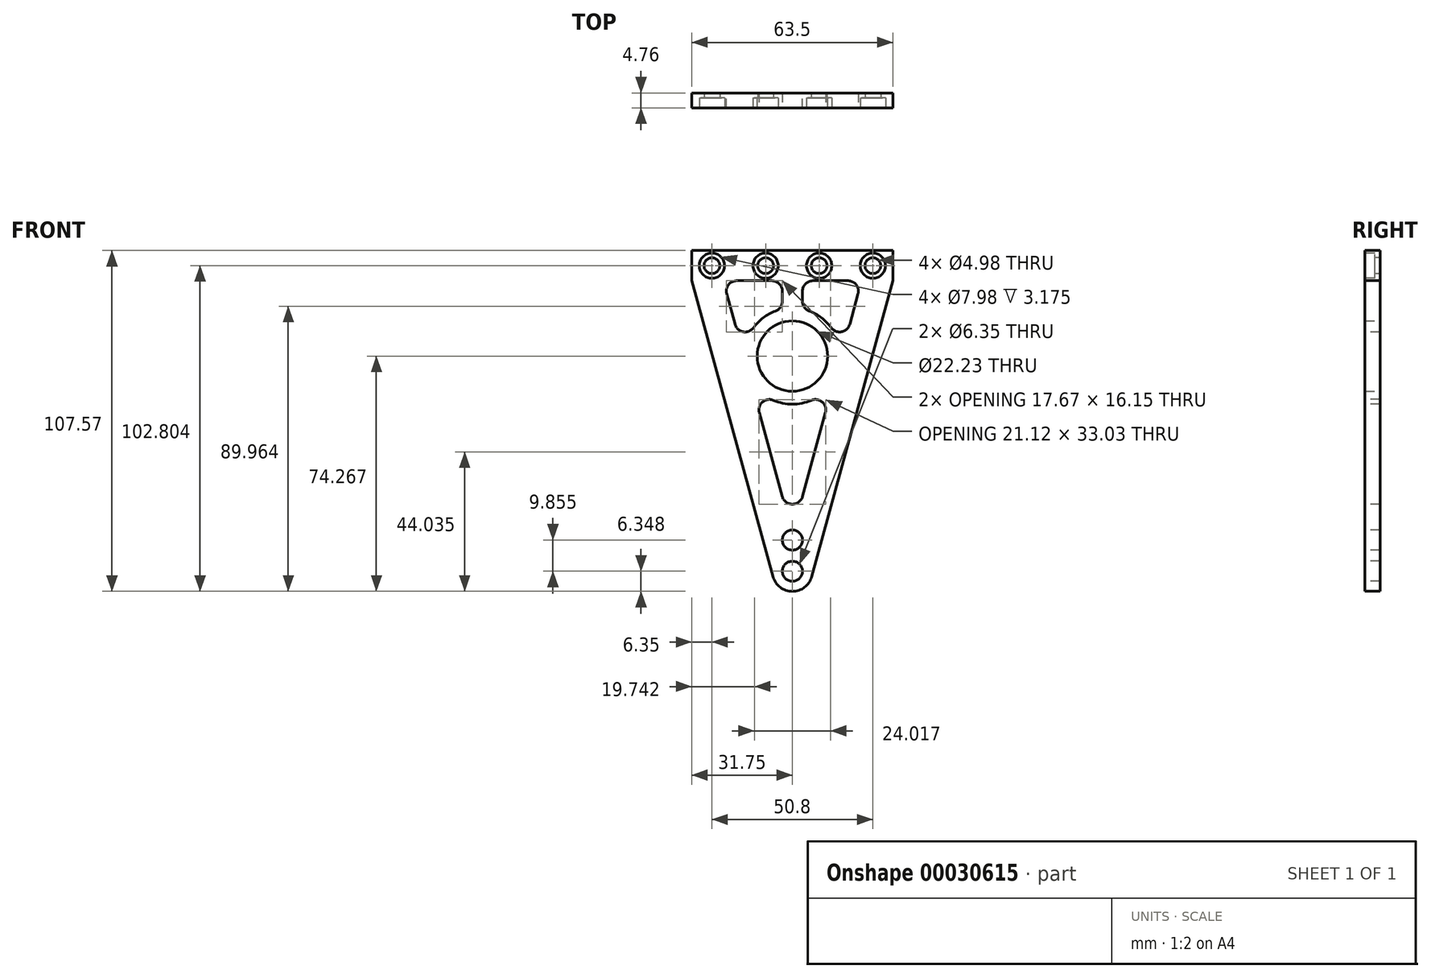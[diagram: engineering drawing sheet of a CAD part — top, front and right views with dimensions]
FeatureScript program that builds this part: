
annotation { "Feature Type Name" : "Feature", "Feature Type Description" : "" }
export const myFeature = defineFeature(function(context is Context, id is Id, definition is map)
    precondition{}
    {
        {
            var Q0;
            Q0=qCreatedBy(makeId("Front.planeOp"),FACE);
            var sketch = newSketch(context, id + "F0", { "sketchPlane" : qUnion([Q0])});
            skLineSegment(sketch, "E0.rect.bottom", {"start": v(31.75, 39.32) * mm, "end": v(-31.75, 39.32) * mm});
            skLineSegment(sketch, "E0.rect.left", {"start": v(31.75, 39.32) * mm, "end": v(31.75, 29.8) * mm});
            skLineSegment(sketch, "E0.rect.right", {"start": v(-31.75, 39.32) * mm, "end": v(-31.75, 29.8) * mm});
            skPoint(sketch, "E0.rect.middle", {"position": v(0, 0) * mm});
            skArc(sketch, "E1", {"start": v(-6.12, -63.58) * mm, "mid": v(0, -68.25) * mm, "end": v(6.12, -63.58) * mm});
            skLineSegment(sketch, "E2", {"start": v(-31.75, 29.8) * mm, "end": v(-6.12, -63.58) * mm});
            skLineSegment(sketch, "E3", {"start": v(31.75, 29.8) * mm, "end": v(6.12, -63.58) * mm});
            skPoint(sketch, "E4.orphan", {"position": v(-31.75, -39.32) * mm});
            skPoint(sketch, "E5.orphan", {"position": v(31.75, -39.32) * mm});
            skCircle(sketch, "E6", {"center": v(0, 6.02) * mm, "radius": 11.11 * mm});
            skPoint(sketch, "E7.orphan", {"position": v(0, 39.32) * mm});
            skSolve(sketch);
        }
        {
            var Q0;
            Q0 = qSketchRegion(id + "F0", true);
            extrude(context, id + "F1", {"entities" : qUnion([Q0]), "depth" : 4.76 * mm});
        }
        {
            var Q0;
            Q0=makeQuery(id+"F1.opExtrude","CAP_FACE",FACE,{"disambiguationData":[OSD([sQuery(id+"F0.wireOp",EDGE,"E0.rect.bottom"),sQuery(id+"F0.wireOp",EDGE,"E0.rect.left"),sQuery(id+"F0.wireOp",EDGE,"E0.rect.right"),sQuery(id+"F0.wireOp",EDGE,"E1"),sQuery(id+"F0.wireOp",EDGE,"E2"),sQuery(id+"F0.wireOp",EDGE,"E3"),sQuery(id+"F0.wireOp",EDGE,"E6")])],"isStart":false});
            var sketch = newSketch(context, id + "F2", { "sketchPlane" : qUnion([Q0])});
            skLineSegment(sketch, "E8.0", {"start": v(-21.87, 29.8) * mm, "end": v(-15.16, 5.34) * mm});
            skLineSegment(sketch, "E9.0", {"start": v(21.87, 29.8) * mm, "end": v(15.16, 5.34) * mm});
            skLineSegment(sketch, "E10.0", {"start": v(21.87, 29.8) * mm, "end": v(3.17, 29.8) * mm});
            skArc(sketch, "E11.0", {"start": v(15.16, 5.34) * mm, "mid": v(12.01, 15.3) * mm, "end": v(3.17, 20.86) * mm});
            skLineSegment(sketch, "E12.trimOffspring", {"start": v(13.38, -1.14) * mm, "end": v(0, -49.9) * mm});
            skLineSegment(sketch, "E13.trimOffspring", {"start": v(-13.38, -1.14) * mm, "end": v(0, -49.9) * mm});
            skArc(sketch, "E14.trimOffspring", {"start": v(-13.38, -1.14) * mm, "mid": v(0, -9.16) * mm, "end": v(13.38, -1.14) * mm});
            skLineSegment(sketch, "E15.rect.left", {"start": v(3.17, 18.15) * mm, "end": v(3.17, 29.8) * mm});
            skLineSegment(sketch, "E15.rect.right", {"start": v(-3.18, 20.86) * mm, "end": v(-3.18, 29.8) * mm});
            skPoint(sketch, "E15.rect.middle", {"position": v(0, 29.8) * mm});
            skPoint(sketch, "E16.orphan", {"position": v(3.17, 41.43) * mm});
            skPoint(sketch, "E17.orphan", {"position": v(-3.18, 41.43) * mm});
            skLineSegment(sketch, "E18.trimOffspring", {"start": v(-3.18, 29.8) * mm, "end": v(-21.87, 29.8) * mm});
            skPoint(sketch, "E15.rect.bottom.end.orphan", {"position": v(-3.18, 18.15) * mm});
            skArc(sketch, "E19.trimOffspring", {"start": v(-3.18, 20.86) * mm, "mid": v(-12.01, 15.3) * mm, "end": v(-15.16, 5.34) * mm});
            skSolve(sketch);
        }
        {
            var Q0;
            Q0=makeQuery(id+"F2.imprint","IMPRINT",FACE,{"disambiguationData":[TD([[makeQuery(id+"F2.imprint","IMPRINT",EDGE,{"derivedFrom":sQuery(id+"F2.wireOp",EDGE,"E8.0")}),1.0]])]});
            var Q1;
            Q1=makeQuery(id+"F2.imprint","IMPRINT",FACE,{"disambiguationData":[TD([[makeQuery(id+"F2.imprint","IMPRINT",EDGE,{"derivedFrom":sQuery(id+"F2.wireOp",EDGE,"E9.0")}),-1.0]])]});
            var Q2;
            Q2=makeQuery(id+"F2.imprint","IMPRINT",FACE,{"disambiguationData":[TD([[makeQuery(id+"F2.imprint","IMPRINT",EDGE,{"derivedFrom":sQuery(id+"F2.wireOp",EDGE,"E12.trimOffspring")}),-1.0]])]});
            extrude(context, id + "F3", {"entities" : qUnion([Q0, Q1, Q2]), "operationType" : NewBodyOperationType.REMOVE, "endBound" : BoundingType.THROUGH_ALL, "oppositeDirection" : true, "depth" : 25.4 * mm});
        }
        {
            var Q0;
            Q0=makeQuery(id+"F3.boolean.opBoolean","COPY",EDGE,{"derivedFrom":makeQuery(id+"F3.opExtrude","SWEPT_EDGE",EDGE,{"disambiguationData":[OSD([sQuery(id+"F2.wireOp",EDGE,"E8.0"),sQuery(id+"F2.wireOp",EDGE,"E18.trimOffspring")])]})});
            var Q1;
            Q1=makeQuery(id+"F3.boolean.opBoolean","COPY",EDGE,{"derivedFrom":makeQuery(id+"F3.opExtrude","SWEPT_EDGE",EDGE,{"disambiguationData":[OSD([sQuery(id+"F2.wireOp",EDGE,"E10.0"),sQuery(id+"F2.wireOp",EDGE,"E15.rect.left")])]})});
            var Q2;
            Q2=makeQuery(id+"F3.boolean.opBoolean","COPY",EDGE,{"derivedFrom":makeQuery(id+"F3.opExtrude","SWEPT_EDGE",EDGE,{"disambiguationData":[OSD([sQuery(id+"F2.wireOp",EDGE,"E15.rect.right"),sQuery(id+"F2.wireOp",EDGE,"E18.trimOffspring")])]})});
            var Q3;
            Q3=makeQuery(id+"F3.boolean.opBoolean","COPY",EDGE,{"derivedFrom":makeQuery(id+"F3.opExtrude","SWEPT_EDGE",EDGE,{"disambiguationData":[OSD([sQuery(id+"F2.wireOp",EDGE,"E9.0"),sQuery(id+"F2.wireOp",EDGE,"E10.0")])]})});
            var Q4;
            Q4=makeQuery(id+"F3.boolean.opBoolean","COPY",EDGE,{"derivedFrom":makeQuery(id+"F3.opExtrude","SWEPT_EDGE",EDGE,{"disambiguationData":[OSD([sQuery(id+"F2.wireOp",EDGE,"E11.0"),sQuery(id+"F2.wireOp",EDGE,"E15.rect.left")])]})});
            var Q5;
            Q5=makeQuery(id+"F3.boolean.opBoolean","COPY",EDGE,{"derivedFrom":makeQuery(id+"F3.opExtrude","SWEPT_EDGE",EDGE,{"disambiguationData":[OSD([sQuery(id+"F2.wireOp",EDGE,"E15.rect.right"),sQuery(id+"F2.wireOp",EDGE,"E19.trimOffspring")])]})});
            var Q6;
            Q6=makeQuery(id+"F3.boolean.opBoolean","COPY",EDGE,{"derivedFrom":makeQuery(id+"F3.opExtrude","SWEPT_EDGE",EDGE,{"disambiguationData":[OSD([sQuery(id+"F2.wireOp",EDGE,"E9.0"),sQuery(id+"F2.wireOp",EDGE,"E11.0")])]})});
            var Q7;
            Q7=makeQuery(id+"F3.boolean.opBoolean","COPY",EDGE,{"derivedFrom":makeQuery(id+"F3.opExtrude","SWEPT_EDGE",EDGE,{"disambiguationData":[OSD([sQuery(id+"F2.wireOp",EDGE,"E8.0"),sQuery(id+"F2.wireOp",EDGE,"E19.trimOffspring")])]})});
            var Q8;
            Q8=makeQuery(id+"F3.boolean.opBoolean","COPY",EDGE,{"derivedFrom":makeQuery(id+"F3.opExtrude","SWEPT_EDGE",EDGE,{"disambiguationData":[OSD([sQuery(id+"F2.wireOp",EDGE,"E13.trimOffspring"),sQuery(id+"F2.wireOp",EDGE,"E14.trimOffspring")])]})});
            var Q9;
            Q9=makeQuery(id+"F3.boolean.opBoolean","COPY",EDGE,{"derivedFrom":makeQuery(id+"F3.opExtrude","SWEPT_EDGE",EDGE,{"disambiguationData":[OSD([sQuery(id+"F2.wireOp",EDGE,"E12.trimOffspring"),sQuery(id+"F2.wireOp",EDGE,"E14.trimOffspring")])]})});
            var Q10;
            Q10=makeQuery(id+"F3.boolean.opBoolean","COPY",EDGE,{"derivedFrom":makeQuery(id+"F3.opExtrude","SWEPT_EDGE",EDGE,{"disambiguationData":[OSD([sQuery(id+"F2.wireOp",EDGE,"E12.trimOffspring"),sQuery(id+"F2.wireOp",EDGE,"E13.trimOffspring")])]})});
            fillet(context, id + "F4", {"entities" : qUnion([Q0, Q1, Q2, Q3, Q4, Q5, Q6, Q7, Q8, Q9, Q10]), "radius" : 3.3 * mm, "tangentPropagation" : true, "allowEdgeOverflow" : false});
        }
        {
            var Q0;
            Q0=makeQuery(id+"F1.opExtrude","CAP_FACE",FACE,{"disambiguationData":[OSD([sQuery(id+"F0.wireOp",EDGE,"E0.rect.bottom"),sQuery(id+"F0.wireOp",EDGE,"E0.rect.left"),sQuery(id+"F0.wireOp",EDGE,"E0.rect.right"),sQuery(id+"F0.wireOp",EDGE,"E1"),sQuery(id+"F0.wireOp",EDGE,"E2"),sQuery(id+"F0.wireOp",EDGE,"E3"),sQuery(id+"F0.wireOp",EDGE,"E6")])],"isStart":false});
            var sketch = newSketch(context, id + "F5", { "sketchPlane" : qUnion([Q0])});
            skCircle(sketch, "E20", {"center": v(0, -61.9) * mm, "radius": 3.18 * mm});
            skCircle(sketch, "E21", {"center": v(0, -52.05) * mm, "radius": 3.18 * mm});
            skPoint(sketch, "E22.start.orphan", {"position": v(0, 39.32) * mm});
            skSolve(sketch);
        }
        {
            var Q0;
            Q0 = qSketchRegion(id + "F5", true);
            extrude(context, id + "F6", {"entities" : qUnion([Q0]), "operationType" : NewBodyOperationType.REMOVE, "endBound" : BoundingType.THROUGH_ALL, "oppositeDirection" : true, "depth" : 25.4 * mm});
        }
        {
            var Q0;
            Q0=makeQuery(id+"F1.opExtrude","CAP_FACE",FACE,{"disambiguationData":[OSD([sQuery(id+"F0.wireOp",EDGE,"E0.rect.bottom"),sQuery(id+"F0.wireOp",EDGE,"E0.rect.left"),sQuery(id+"F0.wireOp",EDGE,"E0.rect.right"),sQuery(id+"F0.wireOp",EDGE,"E1"),sQuery(id+"F0.wireOp",EDGE,"E2"),sQuery(id+"F0.wireOp",EDGE,"E3"),sQuery(id+"F0.wireOp",EDGE,"E6")])],"isStart":false});
            var sketch = newSketch(context, id + "F7", { "sketchPlane" : qUnion([Q0])});
            skLineSegment(sketch, "E23", {"start": v(-31.75, 34.55) * mm, "end": v(31.75, 34.55) * mm});
            skPoint(sketch, "E24", {"position": v(-25.4, 34.55) * mm});
            skPoint(sketch, "E25", {"position": v(-8.46, 34.55) * mm});
            skPoint(sketch, "E26", {"position": v(8.46, 34.55) * mm});
            skPoint(sketch, "E27", {"position": v(25.4, 34.55) * mm});
            skSolve(sketch);
        }
        {
            var Q0;
            Q0=sQuery(id+"F7.wireOp",VERTEX,"E24");
            var Q1;
            Q1=sQuery(id+"F7.wireOp",VERTEX,"E25");
            var Q2;
            Q2=sQuery(id+"F7.wireOp",VERTEX,"E26");
            var Q3;
            Q3=sQuery(id+"F7.wireOp",VERTEX,"E27");
            var Q4;
            Q4=makeQuery(id+"F1.opExtrude","SWEPT_BODY",BODY,{"disambiguationData":[OSD([sQuery(id+"F0.wireOp",EDGE,"E0.rect.bottom"),sQuery(id+"F0.wireOp",EDGE,"E0.rect.left"),sQuery(id+"F0.wireOp",EDGE,"E0.rect.right"),sQuery(id+"F0.wireOp",EDGE,"E1"),sQuery(id+"F0.wireOp",EDGE,"E2"),sQuery(id+"F0.wireOp",EDGE,"E3"),sQuery(id+"F0.wireOp",EDGE,"E6")])]});
            hole(context, id + "F8", {"style" : HoleStyle.C_BORE, "holeDiameter" : 4.98 * mm, "cBoreDiameter" : 7.98 * mm, "cBoreDepth" : 3.17 * mm, "endStyle" : HoleEndStyle.THROUGH, "locations" : qUnion([Q0, Q1, Q2, Q3]), "scope" : qUnion([Q4])});
        }
    });
